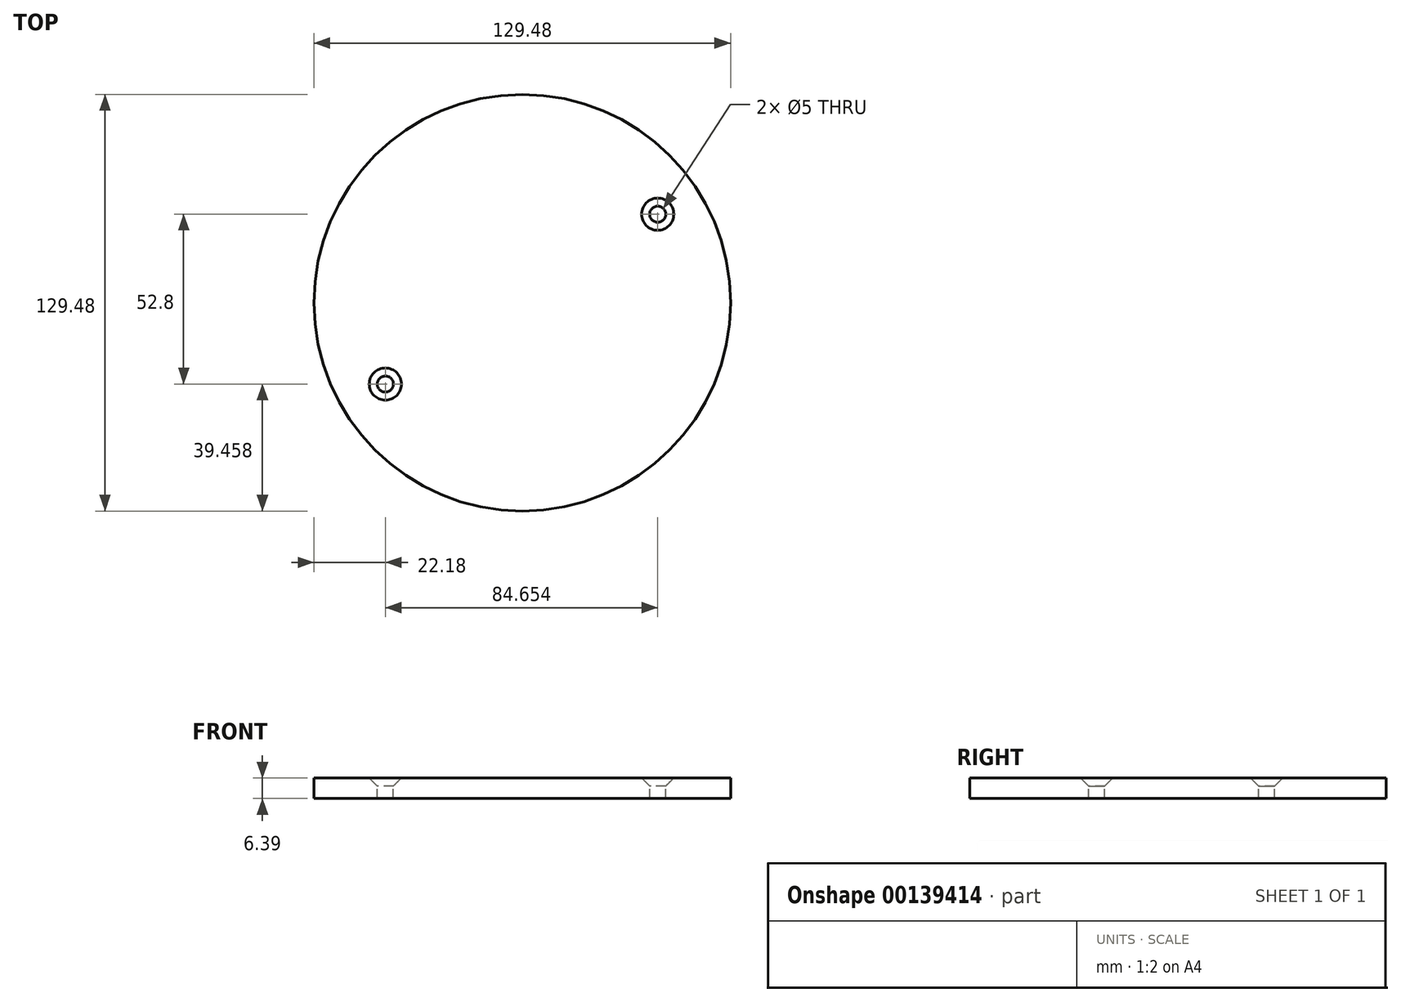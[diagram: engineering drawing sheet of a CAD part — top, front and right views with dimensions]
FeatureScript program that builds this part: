
annotation { "Feature Type Name" : "Feature", "Feature Type Description" : "" }
export const myFeature = defineFeature(function(context is Context, id is Id, definition is map)
    precondition{}
    {
        {
            var Q0;
            Q0=qCreatedBy(makeId("Top.planeOp"),FACE);
            var sketch = newSketch(context, id + "F3", { "sketchPlane" : qUnion([Q0])});
            skCircle(sketch, "E0", {"center": v(0, 0) * mm, "radius": 64.74 * mm});
            skSolve(sketch);
        }
        {
            var Q0;
            Q0=makeQuery(id+"F3.imprint","IMPRINT",FACE,{"disambiguationData":[TD([[makeQuery(id+"F3.imprint","IMPRINT",EDGE,{"derivedFrom":sQuery(id+"F3.wireOp",EDGE,"E0")}),1.0]])]});
            extrude(context, id + "F0", {"entities" : qUnion([Q0]), "depth" : 6.39 * mm});
        }
        {
            var Q0;
            Q0=makeQuery(id+"F0.opExtrude","CAP_FACE",FACE,{"disambiguationData":[OSD([sQuery(id+"F3.wireOp",EDGE,"E0")])],"isStart":false});
            var sketch = newSketch(context, id + "F1", { "sketchPlane" : qUnion([Q0])});
            skCircle(sketch, "E1", {"center": v(42.1, 27.52) * mm, "radius": 3.08 * mm});
            skSolve(sketch);
        }
        {
            var Q0;
            Q0=makeQuery(id+"F1.imprint","IMPRINT",FACE,{"disambiguationData":[TD([[makeQuery(id+"F1.imprint","IMPRINT",EDGE,{"derivedFrom":sQuery(id+"F1.wireOp",EDGE,"E1")}),-1.0]])]});
            var sketch = newSketch(context, id + "F4", { "sketchPlane" : qUnion([Q0])});
            skCircle(sketch, "E2", {"center": v(-42.56, -25.28) * mm, "radius": 3.66 * mm});
            skSolve(sketch);
        }
        {
            var Q0;
            Q0=sQuery(id+"F4.wireOp",VERTEX,"E2.center");
            var Q1;
            Q1=sQuery(id+"F1.wireOp",VERTEX,"E1.center");
            var Q2;
            Q2=makeQuery(id+"F0.opExtrude","SWEPT_BODY",BODY,{"disambiguationData":[OSD([sQuery(id+"F3.wireOp",EDGE,"E0")])]});
            hole(context, id + "F2", {"style" : HoleStyle.C_SINK, "endStyle" : HoleEndStyle.THROUGH, "holeDiameter" : 5 * mm, "cSinkDiameter" : 10 * mm, "cSinkAngle" : 90 * degree, "locations" : qUnion([Q0, Q1]), "scope" : qUnion([Q2]), "isTappedThrough" : true});
        }
    });
